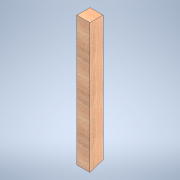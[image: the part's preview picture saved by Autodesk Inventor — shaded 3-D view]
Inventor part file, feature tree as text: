
AUTODESK INVENTOR PART (.ipt)
format: ipt  version: 2020.2 (Build 242310000, 310)  size: 108,544 bytes
history: native  units: in
note: dims shown in document units (in); Inventor stores cm internally (conversion verified against a paired STEP export)
features: extrude x1, sketch x1
ambient origin geometry x8: Origin, YZ Plane, XZ Plane, XY Plane, X Axis, Y Axis, Z Axis, Center Point
bodies: Solid1 (feature_tree)
feature tree (2):
  extrude  "Extrusion1"  TaperAngle=0.0deg  [1 undecoded]
  sketch  "Sketch1"  dims[d3=3.5in d4=0.0in]
note: 1 required parameter value undecoded (feature->parameter linkage not recoverable at this tier; creation-order binding heuristic only, values carry confidence <= 0.55)
